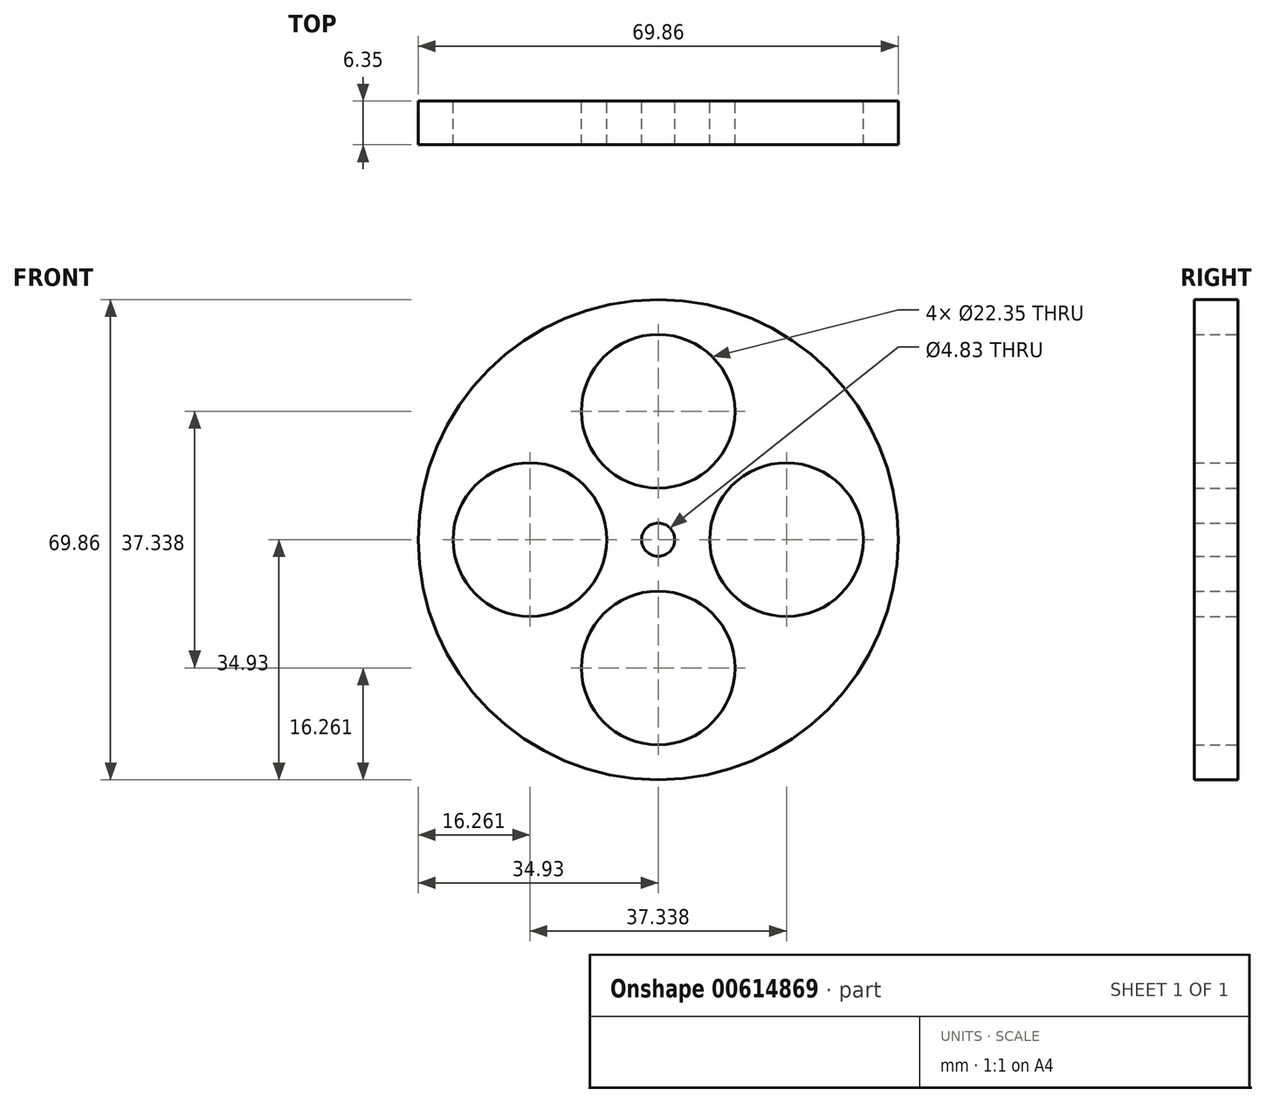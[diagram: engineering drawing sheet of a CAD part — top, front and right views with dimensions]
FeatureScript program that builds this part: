
annotation { "Feature Type Name" : "Feature", "Feature Type Description" : "" }
export const myFeature = defineFeature(function(context is Context, id is Id, definition is map)
    precondition{}
    {
        {
            var Q0;
            Q0=qCreatedBy(makeId("Front.planeOp"),FACE);
            var sketch = newSketch(context, id + "F0", { "sketchPlane" : qUnion([Q0])});
            skCircle(sketch, "E0", {"center": v(0, 0) * mm, "radius": 34.93 * mm});
            skCircle(sketch, "E1", {"center": v(0, 0) * mm, "radius": 2.41 * mm});
            skLineSegment(sketch, "E2", {"start": v(0, -2.41) * mm, "end": v(0, -34.93) * mm});
            skCircle(sketch, "E3", {"center": v(0, -18.67) * mm, "radius": 11.18 * mm});
            skCircle(sketch, "E4.1.0", {"center": v(18.67, 0) * mm, "radius": 11.18 * mm});
            skCircle(sketch, "E4.2.0", {"center": v(0, 18.67) * mm, "radius": 11.18 * mm});
            skCircle(sketch, "E4.3.0", {"center": v(-18.67, 0) * mm, "radius": 11.18 * mm});
            skSolve(sketch);
        }
        {
            var Q0;
            Q0=makeQuery(id+"F0.imprint","IMPRINT",FACE,{"disambiguationData":[TD([[makeQuery(id+"F0.imprint","IMPRINT",EDGE,{"derivedFrom":sQuery(id+"F0.wireOp",EDGE,"E0")}),1.0]])]});
            extrude(context, id + "F1", {"entities" : qUnion([Q0]), "depth" : 6.35 * mm, "offsetDistance" : 25.4 * mm});
        }
        {
            var Q0;
            Q0=sQuery(id+"F0.wireOp",EDGE,"E1");
            extrude(context, id + "F2", {"bodyType" : ToolBodyType.SURFACE, "surfaceEntities" : qUnion([Q0]), "oppositeDirection" : true, "depth" : 2.54 * mm, "offsetDistance" : 25.4 * mm});
        }
    });
